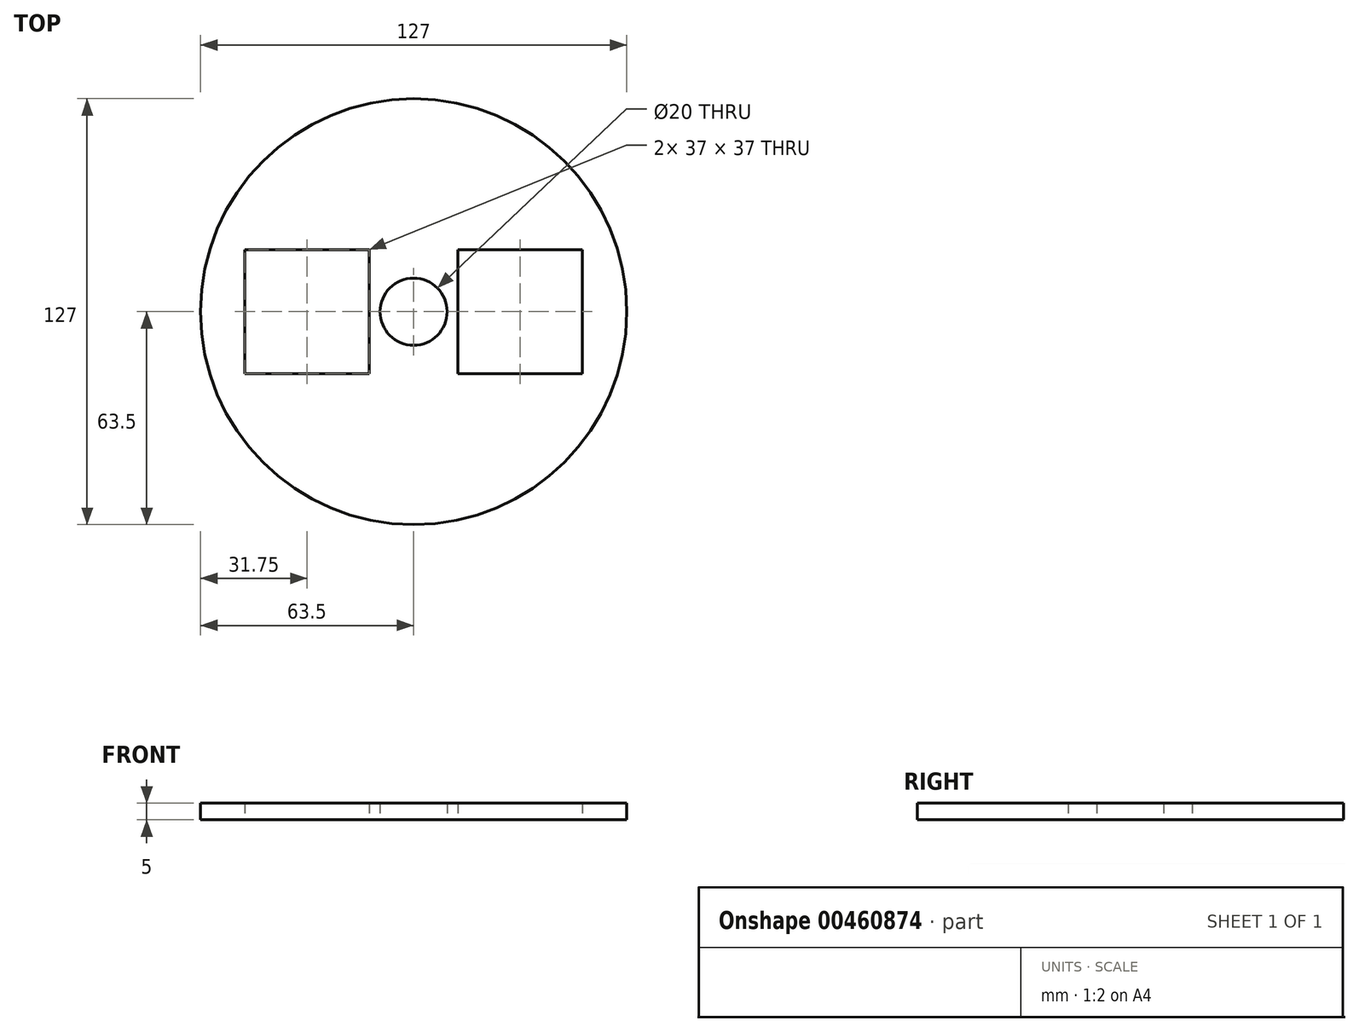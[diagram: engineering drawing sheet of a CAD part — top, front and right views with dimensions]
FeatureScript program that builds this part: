
annotation { "Feature Type Name" : "Feature", "Feature Type Description" : "" }
export const myFeature = defineFeature(function(context is Context, id is Id, definition is map)
    precondition{}
    {
        {
            var Q0;
            Q0=qCreatedBy(makeId("Top.planeOp"),FACE);
            var sketch = newSketch(context, id + "F0", { "sketchPlane" : qUnion([Q0])});
            skCircle(sketch, "E0", {"center": v(0, 0) * mm, "radius": 63.5 * mm});
            skPoint(sketch, "E1", {"position": v(-63.5, 0) * mm});
            skPoint(sketch, "E2", {"position": v(63.5, 0) * mm});
            skCircle(sketch, "E3", {"center": v(0, 0) * mm, "radius": 10 * mm});
            skPoint(sketch, "E4", {"position": v(-31.75, 0) * mm});
            skPoint(sketch, "E5", {"position": v(31.75, 0) * mm});
            skLineSegment(sketch, "E6.bottom", {"start": v(-50.25, 18.5) * mm, "end": v(-13.25, 18.5) * mm});
            skLineSegment(sketch, "E6.top", {"start": v(-50.25, -18.5) * mm, "end": v(-13.25, -18.5) * mm});
            skLineSegment(sketch, "E6.left", {"start": v(-50.25, 18.5) * mm, "end": v(-50.25, -18.5) * mm});
            skLineSegment(sketch, "E6.right", {"start": v(-13.25, 18.5) * mm, "end": v(-13.25, -18.5) * mm});
            skLineSegment(sketch, "E7.bottom", {"start": v(50.25, 18.5) * mm, "end": v(13.25, 18.5) * mm});
            skLineSegment(sketch, "E7.top", {"start": v(50.25, -18.5) * mm, "end": v(13.25, -18.5) * mm});
            skLineSegment(sketch, "E7.left", {"start": v(50.25, 18.5) * mm, "end": v(50.25, -18.5) * mm});
            skLineSegment(sketch, "E7.right", {"start": v(13.25, 18.5) * mm, "end": v(13.25, -18.5) * mm});
            skLineSegment(sketch, "E8", {"start": v(-63.5, 0) * mm, "end": v(0, 0) * mm, "construction": true});
            skLineSegment(sketch, "E9", {"start": v(0, 0) * mm, "end": v(63.5, 0) * mm, "construction": true});
            skPoint(sketch, "E10", {"position": v(0, 63.5) * mm});
            skPoint(sketch, "E11", {"position": v(0, -63.5) * mm});
            skPoint(sketch, "E12", {"position": v(-63.5, 63.5) * mm});
            skPoint(sketch, "E13", {"position": v(-63.5, -63.5) * mm});
            skSolve(sketch);
        }
        {
            var Q0;
            Q0 = qSketchRegion(id + "F0", true);
            extrude(context, id + "F1", {"entities" : qUnion([Q0]), "depth" : 5 * mm});
        }
    });
